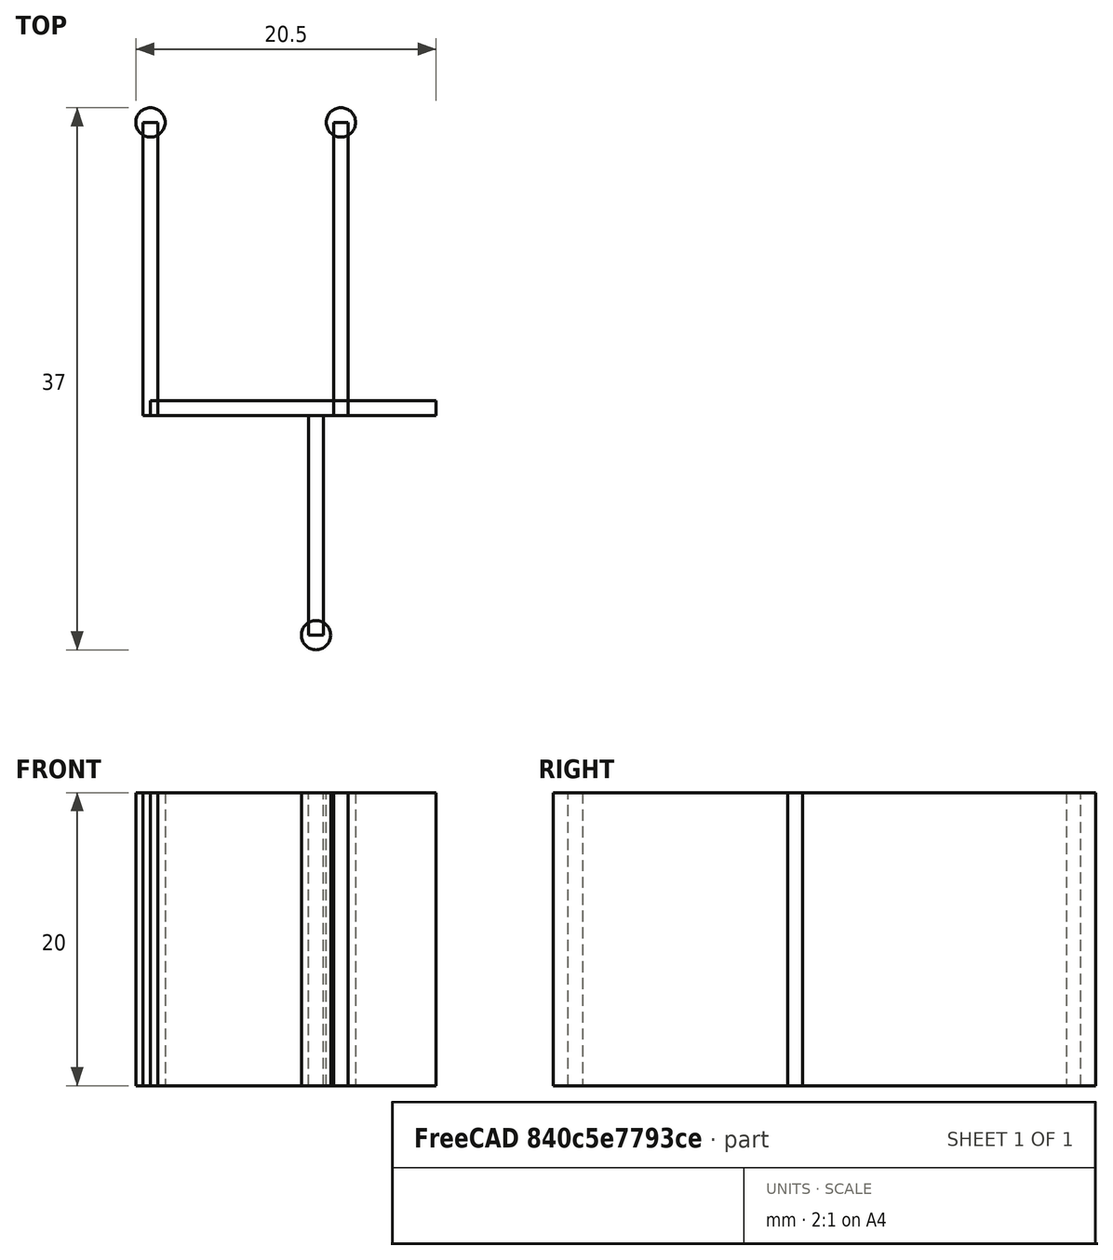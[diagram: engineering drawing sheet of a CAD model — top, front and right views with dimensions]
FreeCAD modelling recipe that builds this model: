
FCSTD DOCUMENT  (FreeCAD 1.0R39109 (Git))
Label: usb-holder-desk-v2.mirror
License: All rights reserved
LicenseURL: http://en.wikipedia.org/wiki/All_rights_reserved
objects: Part::Mirroring×7, Part::Box×4, Part::Cylinder×3, Sketcher::SketchObject×1
note: 16 computed .brp shape members not serialized (recipe doc carries the construction recipe); baked Part::Feature solids carry a one-line shape summary decoded from their .brp

FEATURE [Sketcher::SketchObject] Sketch
  ArcFitTolerance = 0
  FullyConstrained = true
  MakeInternals = false
FEATURE [Part::Box] Box  label="Cube"
  AttacherType = Attacher::AttachEngine3D
  Height = 20
  Length = 19.5
  Width = 1
FEATURE [Part::Box] Box001  label="Cube001"
  AttacherType = Attacher::AttachEngine3D
  Height = 20
  Length = 1
  Placement = pos=(6,0,0) rot=(0,0,1;0rad)
  Width = 20
FEATURE [Part::Box] Box002  label="Cube002"
  AttacherType = Attacher::AttachEngine3D
  Height = 20
  Length = 1
  Placement = pos=(19,0,0) rot=(0,0,1;0rad)
  Width = 20
FEATURE [Part::Cylinder] Cylinder
  Angle = 360
  AttacherType = Attacher::AttachEngine3D
  FirstAngle = 0
  Height = 20
  Placement = pos=(6.5,20,0) rot=(0,0,1;0rad)
  Radius = 1
  SecondAngle = 0
FEATURE [Part::Cylinder] Cylinder001
  Angle = 360
  AttacherType = Attacher::AttachEngine3D
  FirstAngle = 0
  Height = 20
  Placement = pos=(19.5,20,0) rot=(0,0,1;0rad)
  Radius = 1
  SecondAngle = 0
FEATURE [Part::Box] Box003  label="Cube003"
  AttacherType = Attacher::AttachEngine3D
  Height = 20
  Length = 1
  Placement = pos=(7.7,-15,0) rot=(0,0,1;0rad)
  Width = 15
FEATURE [Part::Cylinder] Cylinder002
  Angle = 360
  AttacherType = Attacher::AttachEngine3D
  FirstAngle = 0
  Height = 20
  Placement = pos=(8.2,-15,0) rot=(0,0,1;0rad)
  Radius = 1
  SecondAngle = 0
FEATURE [Part::Mirroring] Part__Mirroring  label="Cube (Mirror #1)"
  Base = (0,0,0)
  Normal = (1,0,0)
  Source = -> Box
FEATURE [Part::Mirroring] Part__Mirroring001  label="Cube001 (Mirror #2)"
  Base = (0,0,0)
  Normal = (1,0,0)
  Source = -> Box001
FEATURE [Part::Mirroring] Part__Mirroring002  label="Cube002 (Mirror #3)"
  Base = (0,0,0)
  Normal = (1,0,0)
  Source = -> Box002
FEATURE [Part::Mirroring] Part__Mirroring003  label="Cylinder (Mirror #4)"
  Base = (0,0,0)
  Normal = (1,0,0)
  Source = -> Cylinder
FEATURE [Part::Mirroring] Part__Mirroring004  label="Cylinder001 (Mirror #5)"
  Base = (0,0,0)
  Normal = (1,0,0)
  Source = -> Cylinder001
FEATURE [Part::Mirroring] Part__Mirroring005  label="Cube003 (Mirror #6)"
  Base = (0,0,0)
  Normal = (1,0,0)
  Source = -> Box003
FEATURE [Part::Mirroring] Part__Mirroring006  label="Cylinder002 (Mirror #7)"
  Base = (0,0,0)
  Normal = (1,0,0)
  Source = -> Cylinder002
